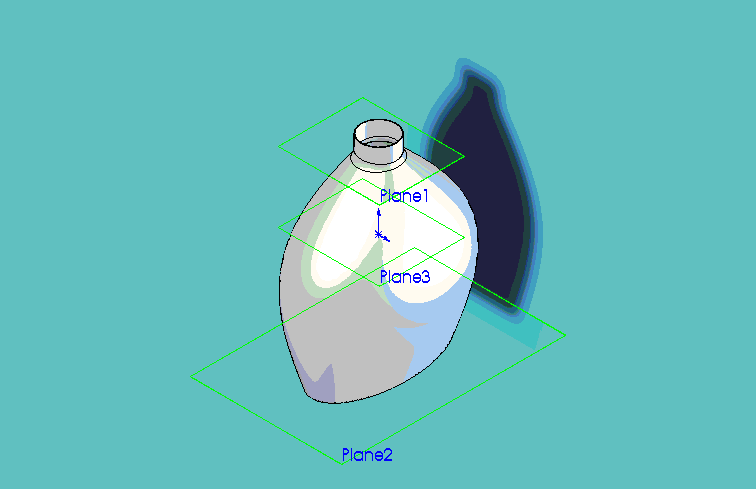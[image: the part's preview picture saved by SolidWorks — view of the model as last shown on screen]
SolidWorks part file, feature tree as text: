
SOLIDWORKS PART (.sldprt)
format: sldprt  version: not decoded by parser v0  size: 446,976 bytes
history: native  units: mm
features: plane x6, sketch x4, material x1, extrude x1, fillet x1, shell x1 (+10 scaffold rows collapsed)
feature tree (24):
  scaffold x10  (default folders/planes/origin — collapsed)
  material  "Material <not specified>"
  plane  "Frontal"
  plane  "Horizontal"
  plane  "Profile"
  plane  "Plane1"  Offset=50.8mm
  plane  "Plane2"  Offset=76.2mm
  plane  "Plane3"  Offset=50.8mm
  sketch  "Sketch6"  dims[D1=38.1mm]
  sketch  "Sketch7"  dims[D1=38.1mm]
  sketch  "Sketch8"  dims[D1=25.4mm]
  sketch  "Sketch9"
  extrude  "Extrude1"  Depth=12.7mm
  fillet  "Fillet1"  Radius=6.35mm
  shell  "Shell1"  Thickness=0.508mm
decode coverage: 6 of 7 modeling features carry decoded parameters
note: suppression state not decoded; provenance and decode notes live in map.json
